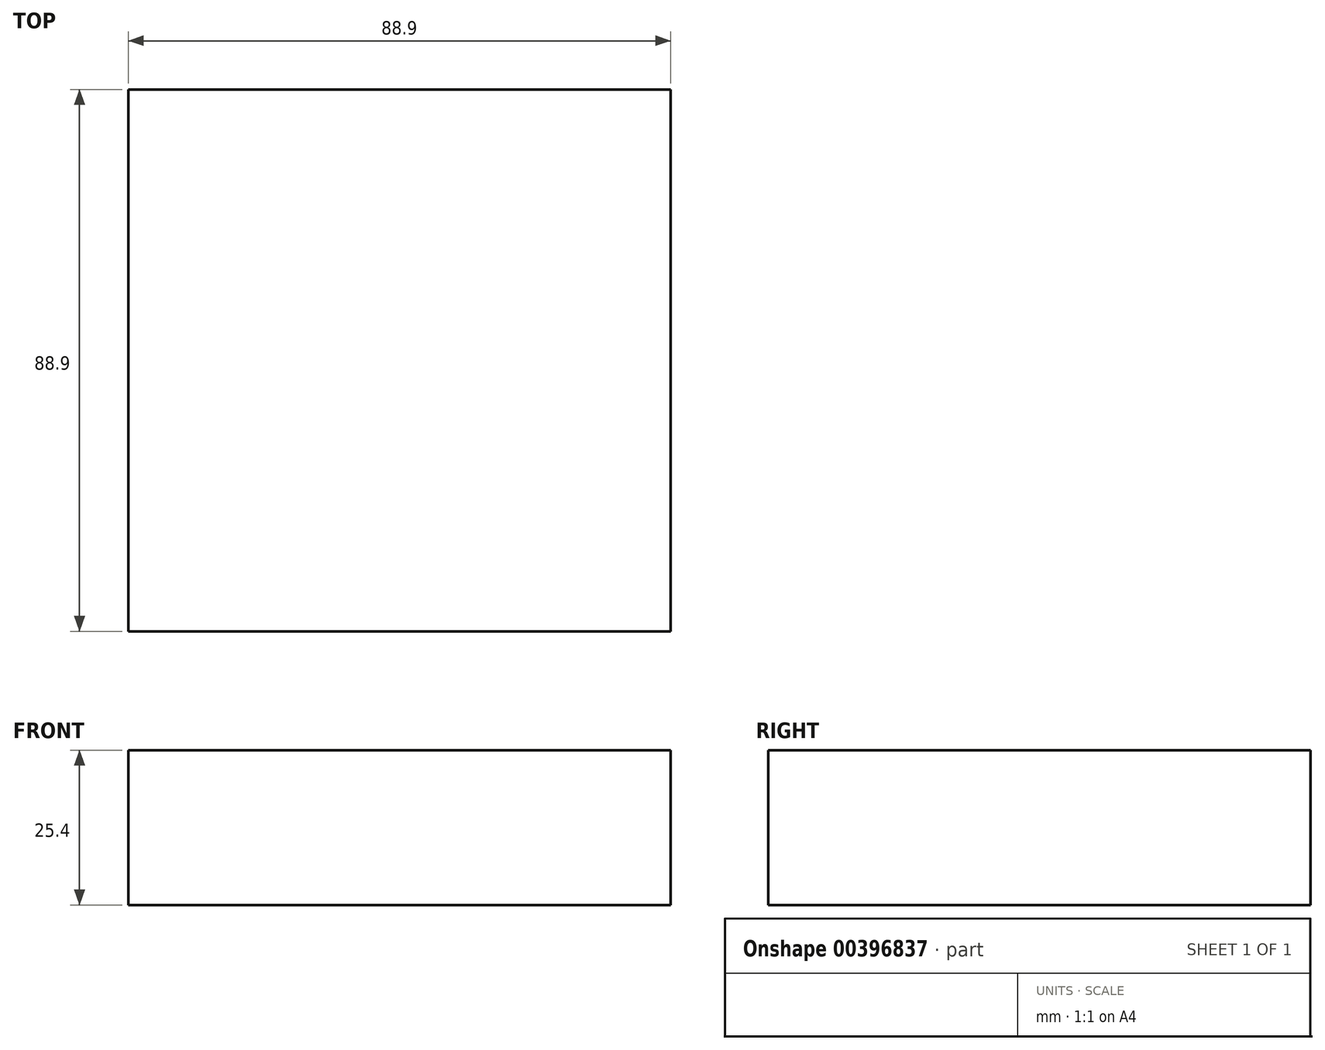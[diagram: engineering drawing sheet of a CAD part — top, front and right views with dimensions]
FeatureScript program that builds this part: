
annotation { "Feature Type Name" : "Feature", "Feature Type Description" : "" }
export const myFeature = defineFeature(function(context is Context, id is Id, definition is map)
    precondition{}
    {
        {
            var Q0;
            Q0=qCreatedBy(makeId("Top.planeOp"),FACE);
            var sketch = newSketch(context, id + "F0", { "sketchPlane" : qUnion([Q0])});
            skLineSegment(sketch, "E0.bottom", {"start": v(-44.45, 44.45) * mm, "end": v(44.45, 44.45) * mm});
            skLineSegment(sketch, "E0.top", {"start": v(-44.45, -44.45) * mm, "end": v(44.45, -44.45) * mm});
            skLineSegment(sketch, "E0.left", {"start": v(-44.45, 44.45) * mm, "end": v(-44.45, -44.45) * mm});
            skLineSegment(sketch, "E0.right", {"start": v(44.45, 44.45) * mm, "end": v(44.45, -44.45) * mm});
            skPoint(sketch, "E0.middle", {"position": v(0, 0) * mm});
            skSolve(sketch);
        }
        {
            var Q0;
            Q0=makeQuery(id+"F0.imprint","IMPRINT",FACE,{"disambiguationData":[TD([[makeQuery(id+"F0.imprint","IMPRINT",EDGE,{"derivedFrom":sQuery(id+"F0.wireOp",EDGE,"E0.bottom")}),-1.0]])]});
            extrude(context, id + "F1", {"entities" : qUnion([Q0]), "depth" : 25.4 * mm});
        }
    });
